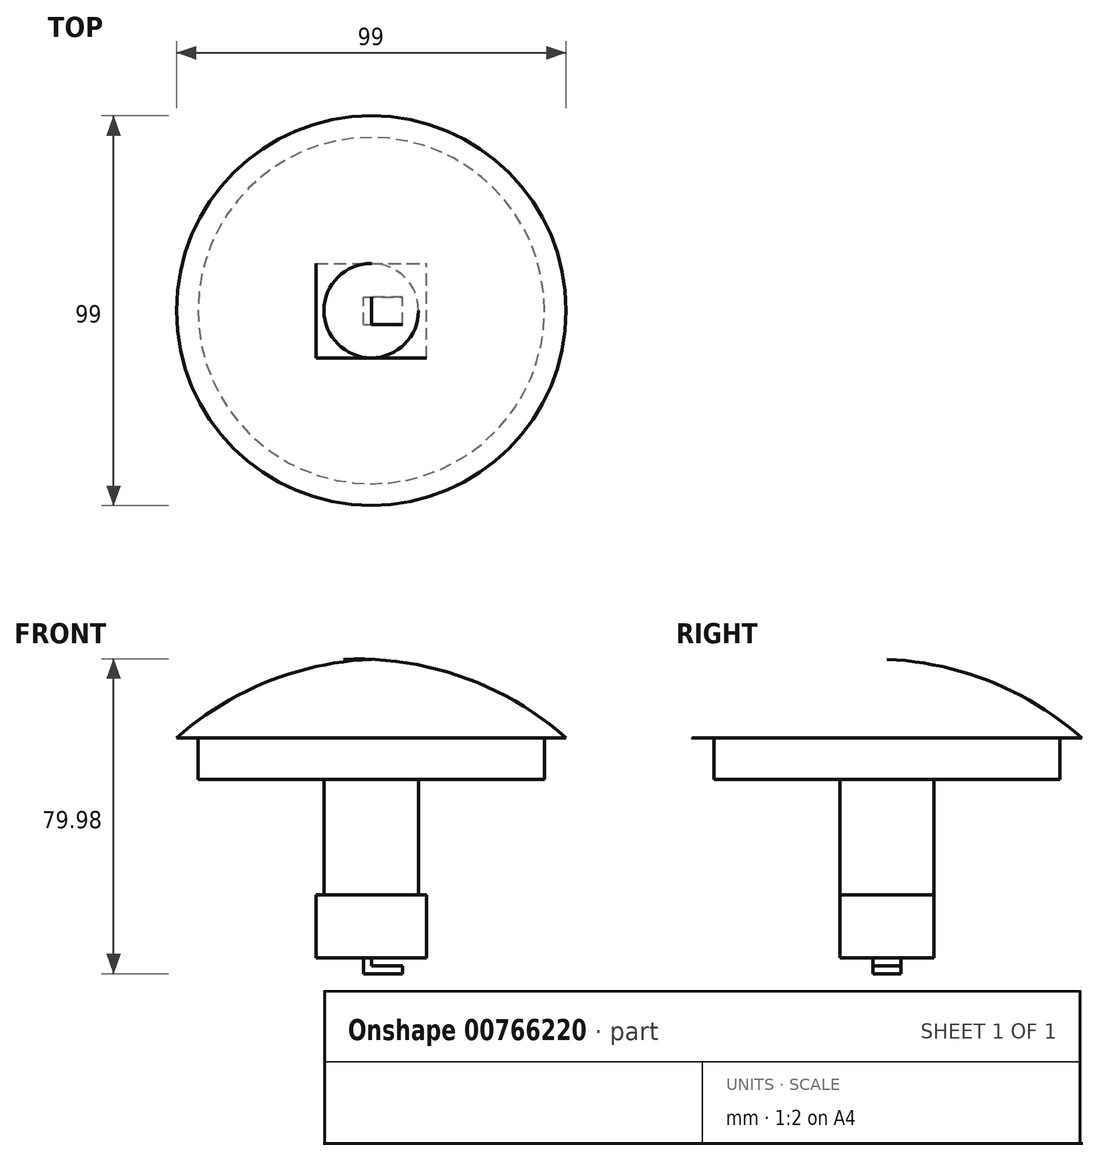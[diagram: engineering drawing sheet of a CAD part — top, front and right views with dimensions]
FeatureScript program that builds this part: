
annotation { "Feature Type Name" : "Feature", "Feature Type Description" : "" }
export const myFeature = defineFeature(function(context is Context, id is Id, definition is map)
    precondition{}
    {
        {
            var Q0;
            Q0=qCreatedBy(makeId("Top.planeOp"),FACE);
            var sketch = newSketch(context, id + "F0", { "sketchPlane" : qUnion([Q0])});
            skCircle(sketch, "E0", {"center": v(0, 0) * mm, "radius": 44 * mm});
            skCircle(sketch, "E1", {"center": v(0, 0) * mm, "radius": 12 * mm});
            skSolve(sketch);
        }
        {
            var Q0;
            Q0=makeQuery(id+"F0.imprint","IMPRINT",FACE,{"disambiguationData":[TD([[makeQuery(id+"F0.imprint","IMPRINT",EDGE,{"derivedFrom":sQuery(id+"F0.wireOp",EDGE,"E1")}),1.0]])]});
            extrude(context, id + "F1", {"entities" : qUnion([Q0]), "depth" : -29.4 * mm, "offsetDistance" : 25 * mm});
        }
        {
            var Q0;
            Q0=makeQuery(id+"F0.imprint","IMPRINT",FACE,{"disambiguationData":[TD([[makeQuery(id+"F0.imprint","IMPRINT",EDGE,{"derivedFrom":sQuery(id+"F0.wireOp",EDGE,"E1")}),1.0]])]});
            var Q1;
            Q1=makeQuery(id+"F0.imprint","IMPRINT",FACE,{"disambiguationData":[TD([[makeQuery(id+"F0.imprint","IMPRINT",EDGE,{"derivedFrom":sQuery(id+"F0.wireOp",EDGE,"E0")}),1.0]])]});
            extrude(context, id + "F2", {"entities" : qUnion([Q0, Q1]), "operationType" : NewBodyOperationType.ADD, "depth" : (10.5) * mm, "offsetDistance" : 25 * mm});
        }
        {
            var Q0;
            Q0=qCreatedBy(makeId("Front.planeOp"),FACE);
            var sketch = newSketch(context, id + "F3", { "sketchPlane" : qUnion([Q0])});
            skLineSegment(sketch, "E2", {"start": v(0, 10.5) * mm, "end": v(-49.5, 10.5) * mm});
            skLineSegment(sketch, "E3", {"start": v(0, 10.5) * mm, "end": v(0, 30.5) * mm});
            skArc(sketch, "E4", {"start": v(0, 30.5) * mm, "mid": v(-26.47, 24.75) * mm, "end": v(-49.5, 10.5) * mm});
            skSolve(sketch);
        }
        {
            var Q0;
            Q0=makeQuery(id+"F3.imprint","IMPRINT",FACE,{"disambiguationData":[TD([[makeQuery(id+"F3.imprint","IMPRINT",EDGE,{"derivedFrom":sQuery(id+"F3.wireOp",EDGE,"E2")}),-1.0]])]});
            var Q1;
            Q1=sQuery(id+"F3.wireOp",EDGE,"E3");
            revolve(context, id + "F4", {"operationType" : NewBodyOperationType.ADD, "surfaceOperationType" : NewSurfaceOperationType.NEW, "entities" : qUnion([Q0]), "axis" : qUnion([Q1]), "revolveType" : RevolveType.FULL});
        }
        {
            var Q0;
            Q0=makeQuery(id+"F1.opExtrude","CAP_FACE",FACE,{"disambiguationData":[OSD([sQuery(id+"F0.wireOp",EDGE,"E1")])],"isStart":false});
            var sketch = newSketch(context, id + "F5", { "sketchPlane" : qUnion([Q0])});
            skLineSegment(sketch, "E5", {"start": v(0, 12) * mm, "end": v(14, 12) * mm});
            skLineSegment(sketch, "E6", {"start": v(14, 12) * mm, "end": v(14, -12) * mm});
            skLineSegment(sketch, "E7", {"start": v(0, -12) * mm, "end": v(14, -12) * mm});
            skLineSegment(sketch, "E8", {"start": v(0, 12) * mm, "end": v(0, -12) * mm});
            skSolve(sketch);
        }
        {
            var Q0;
            Q0 = qSketchRegion(id + "F5", true);
            extrude(context, id + "F6", {"entities" : qUnion([Q0]), "depth" : 16 * mm, "offsetDistance" : 25 * mm});
        }
        {
            var Q0;
            Q0=makeQuery(id+"F6.opExtrude","SWEPT_BODY",BODY,{"disambiguationData":[OSD([sQuery(id+"F5.wireOp",EDGE,"E5"),sQuery(id+"F5.wireOp",EDGE,"E6"),sQuery(id+"F5.wireOp",EDGE,"E7"),sQuery(id+"F5.wireOp",EDGE,"E8")])]});
            var Q1;
            Q1=makeQuery(id+"F6.opExtrude","SWEPT_FACE",FACE,{"disambiguationData":[OSD([sQuery(id+"F5.wireOp",EDGE,"E8")])]});
            mirror(context, id + "F7", {"operationType" : NewBodyOperationType.ADD, "entities" : qUnion([Q0]), "mirrorPlane" : qUnion([Q1])});
        }
        {
            var Q0;
            {var subQ0=makeQuery(id+"F6.opExtrude","CAP_FACE",FACE,{"disambiguationData":[OSD([sQuery(id+"F5.wireOp",EDGE,"E5"),sQuery(id+"F5.wireOp",EDGE,"E6"),sQuery(id+"F5.wireOp",EDGE,"E7"),sQuery(id+"F5.wireOp",EDGE,"E8")])],"isStart":false});Q0=makeQuery(id+"F7.boolean.opBoolean","MERGE",FACE,{"derivedFrom":[subQ0,makeQuery(id+"F7.opPattern","COPY",FACE,{"derivedFrom":subQ0,"instanceName":"1"})]});}
            var sketch = newSketch(context, id + "F8", { "sketchPlane" : qUnion([Q0])});
            skLineSegment(sketch, "E9.bottom", {"start": v(-2, 3.5) * mm, "end": v(0, 3.5) * mm});
            skLineSegment(sketch, "E9.top", {"start": v(-2, -3.5) * mm, "end": v(0, -3.5) * mm});
            skLineSegment(sketch, "E9.left", {"start": v(-2, 3.5) * mm, "end": v(-2, -3.5) * mm});
            skLineSegment(sketch, "E9.right", {"start": v(0, 3.5) * mm, "end": v(0, -3.5) * mm});
            skLineSegment(sketch, "E10", {"start": v(0, 12) * mm, "end": v(0, -12) * mm, "construction": true});
            skPoint(sketch, "E11", {"position": v(0, 0) * mm});
            skSolve(sketch);
        }
        {
            var Q0;
            Q0=makeQuery(id+"F8.imprint","IMPRINT",FACE,{"disambiguationData":[TD([[makeQuery(id+"F8.imprint","IMPRINT",EDGE,{"derivedFrom":sQuery(id+"F8.wireOp",EDGE,"E9.bottom")}),-1.0]])]});
            extrude(context, id + "F9", {"entities" : qUnion([Q0]), "operationType" : NewBodyOperationType.ADD, "depth" : 4 * mm, "offsetDistance" : 25 * mm});
        }
        {
            var Q0;
            Q0=makeQuery(id+"F9.opExtrude","SWEPT_FACE",FACE,{"disambiguationData":[OSD([sQuery(id+"F8.wireOp",EDGE,"E9.right")])]});
            var sketch = newSketch(context, id + "F10", { "sketchPlane" : qUnion([Q0])});
            skLineSegment(sketch, "E12.bottom", {"start": v(-3.5, -49.4) * mm, "end": v(3.5, -49.4) * mm});
            skLineSegment(sketch, "E12.top", {"start": v(-3.5, -47.4) * mm, "end": v(3.5, -47.4) * mm});
            skLineSegment(sketch, "E12.left", {"start": v(-3.5, -49.4) * mm, "end": v(-3.5, -47.4) * mm});
            skLineSegment(sketch, "E12.right", {"start": v(3.5, -49.4) * mm, "end": v(3.5, -47.4) * mm});
            skSolve(sketch);
        }
        {
            var Q0;
            Q0=makeQuery(id+"F10.imprint","IMPRINT",FACE,{"disambiguationData":[TD([[makeQuery(id+"F10.imprint","IMPRINT",EDGE,{"derivedFrom":sQuery(id+"F10.wireOp",EDGE,"E12.bottom")}),1.0]])]});
            extrude(context, id + "F11", {"entities" : qUnion([Q0]), "operationType" : NewBodyOperationType.ADD, "depth" : 8 * mm, "offsetDistance" : 25 * mm});
        }
    });
